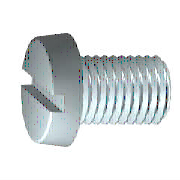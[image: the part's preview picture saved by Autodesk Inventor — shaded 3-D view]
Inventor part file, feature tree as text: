
AUTODESK INVENTOR PART (.ipt)
format: ipt  version: 2023.3 (Build 273359000, 359)  size: 188,416 bytes
history: native  units: mm (DEFAULTED — no unit token found)
features: sketch x2, other x1, extrude x1, plane x1
ambient origin geometry x7: Origin, YZ Plane, XZ Plane, X Axis, Y Axis, Z Axis, Center Point
bodies: Solid1 (feature_tree)
feature tree (5):
  other  "Körper"
  sketch  "Skizze2"  dims[d2=0.306825mm d3=2.0mm d4=3.0mm d5=2.6935mm d8=90.0deg d7=0.0mm d9=5.5mm d10=0.872665mm d11=0.8mm d12=5.5mm d14=0.1mm d15=3.0mm d16=0.0mm d17=0.306725mm d18=0.306825mm d19=0.85mm d20=0.0mm d36=45.0deg d37=0.0mm d39=0.0mm]
  extrude  "Loch"  Depth=3.0mm
  plane  "Work Plane1"
  sketch  "Skizze1"  dims[d0=4.0mm d1=3.0mm]
